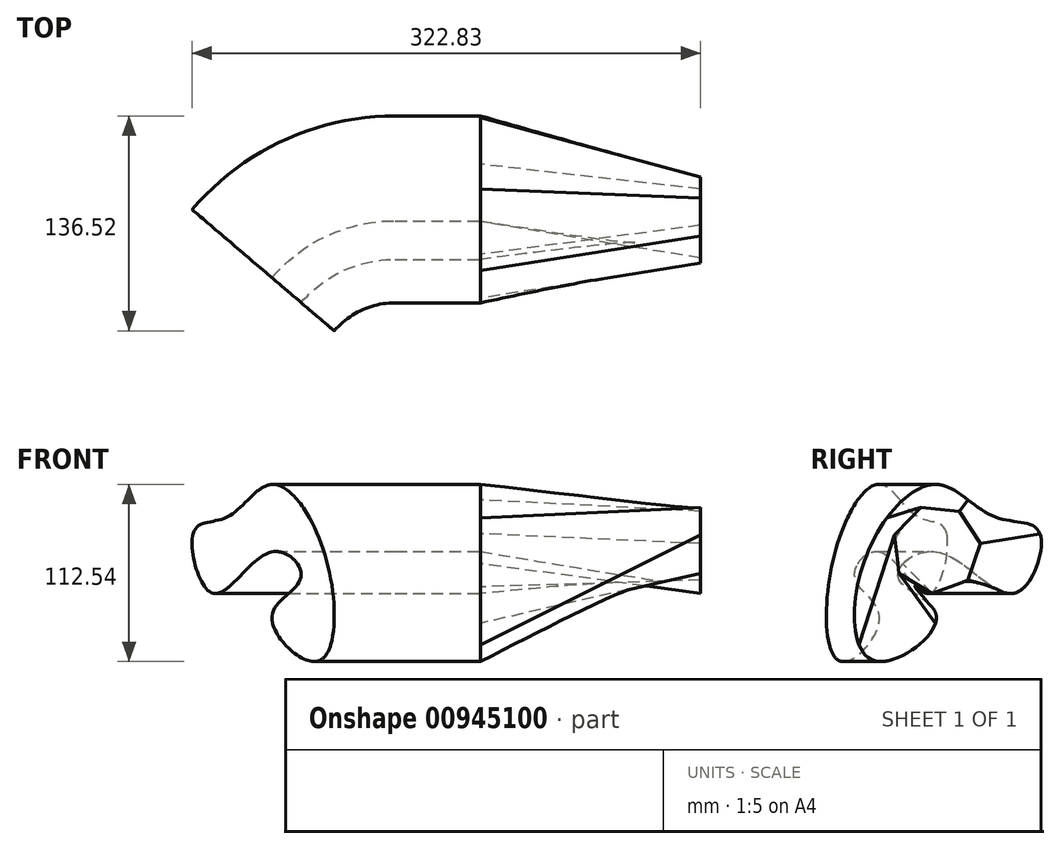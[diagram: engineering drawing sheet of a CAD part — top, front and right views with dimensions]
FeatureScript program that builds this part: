
annotation { "Feature Type Name" : "Feature", "Feature Type Description" : "" }
export const myFeature = defineFeature(function(context is Context, id is Id, definition is map)
    precondition{}
    {
        {
            var Q0;
            Q0=qCreatedBy(makeId("Right.planeOp"),FACE);
            cPlane(context, id + "F0", {"entities" : qUnion([Q0]), "cplaneType" : CPlaneType.OFFSET, "offset" : 139.7 * mm, "width" : 152.4 * mm, "height" : 152.4 * mm});
        }
        {
            var Q0;
            Q0=qCreatedBy(id+"F0.planeOp",FACE);
            var sketch = newSketch(context, id + "F1", { "sketchPlane" : qUnion([Q0])});
            skCircle(sketch, "E0.cCircle", {"center": v(0, 10) * mm, "radius": 25.4 * mm, "construction": true});
            skLineSegment(sketch, "E0.0", {"start": v(14.66, 34.07) * mm, "end": v(27.97, 13.54) * mm});
            skLineSegment(sketch, "E0.1", {"start": v(27.97, 13.54) * mm, "end": v(20.21, -9.66) * mm});
            skLineSegment(sketch, "E0.2", {"start": v(20.21, -9.66) * mm, "end": v(-2.76, -18.06) * mm});
            skLineSegment(sketch, "E0.3", {"start": v(-2.76, -18.06) * mm, "end": v(-23.66, -5.34) * mm});
            skLineSegment(sketch, "E0.4", {"start": v(-23.66, -5.34) * mm, "end": v(-26.74, 18.93) * mm});
            skLineSegment(sketch, "E0.5", {"start": v(-26.74, 18.93) * mm, "end": v(-9.68, 36.47) * mm});
            skLineSegment(sketch, "E0.6", {"start": v(-9.68, 36.47) * mm, "end": v(14.66, 34.07) * mm});
            skPoint(sketch, "E0.0.midPoint", {"position": v(21.32, 23.8) * mm});
            skSolve(sketch);
        }
        {
            var Q0;
            Q0=qCreatedBy(makeId("Right.planeOp"),FACE);
            var sketch = newSketch(context, id + "F2", { "sketchPlane" : qUnion([Q0])});
            skFitSpline(sketch, "E1", {"points": [v(37.5, 30.34) * mm, v(0, 51.13) * mm, v(-46.55, 0) * mm, v(-38.18, -61.13) * mm, v(0, -32.58) * mm, v(-24.14, -8.1) * mm, v(0, 8.26) * mm, v(49.85, -17.86) * mm, v(65.44, 20.58) * mm, v(37.5, 30.34) * mm]});
            skSolve(sketch);
        }
        {
            var Q0;
            Q0=makeQuery(id+"F1.imprint","IMPRINT",FACE,{"disambiguationData":[TD([[makeQuery(id+"F1.imprint","IMPRINT",EDGE,{"derivedFrom":sQuery(id+"F1.wireOp",EDGE,"E0.0")}),-1.0]])]});
            var Q1;
            Q1=makeQuery(id+"F2.imprint","IMPRINT",FACE,{"disambiguationData":[TD([[makeQuery(id+"F2.imprint","IMPRINT",EDGE,{"derivedFrom":sQuery(id+"F2.wireOp",EDGE,"E1")}),1.0]])]});
            loft(context, id + "F3", {"sheetProfilesArray" : [{ "sheetProfileEntities" : qUnion([Q0]) }, { "sheetProfileEntities" : qUnion([Q1]) }]});
        }
        {
            var Q0;
            Q0=qCreatedBy(makeId("Top.planeOp"),FACE);
            var sketch = newSketch(context, id + "F4", { "sketchPlane" : qUnion([Q0])});
            skLineSegment(sketch, "E2", {"start": v(0, 0) * mm, "end": v(-54.19, 0) * mm});
            skArc(sketch, "E3", {"start": v(-54.19, 0) * mm, "mid": v(-97.27, -9.46) * mm, "end": v(-132.42, -36.08) * mm});
            skSolve(sketch);
        }
        {
            var Q0;
            Q0=makeQuery(id+"F3.opLoft","CAP_FACE",FACE,{"disambiguationData":[OSD([makeQuery(id+"F2.imprint","IMPRINT",FACE,{"disambiguationData":[TD([[makeQuery(id+"F2.imprint","IMPRINT",EDGE,{"derivedFrom":sQuery(id+"F2.wireOp",EDGE,"E1")}),1.0]])]})])],"isStart":true});
            var Q1;
            Q1=sQuery(id+"F4.wireOp",EDGE,"E3");
            var Q2;
            Q2=sQuery(id+"F4.wireOp",EDGE,"E2");
            sweep(context, id + "F5", {"operationType" : NewBodyOperationType.ADD, "profiles" : qUnion([Q0]), "path" : qUnion([Q1, Q2])});
        }
    });
